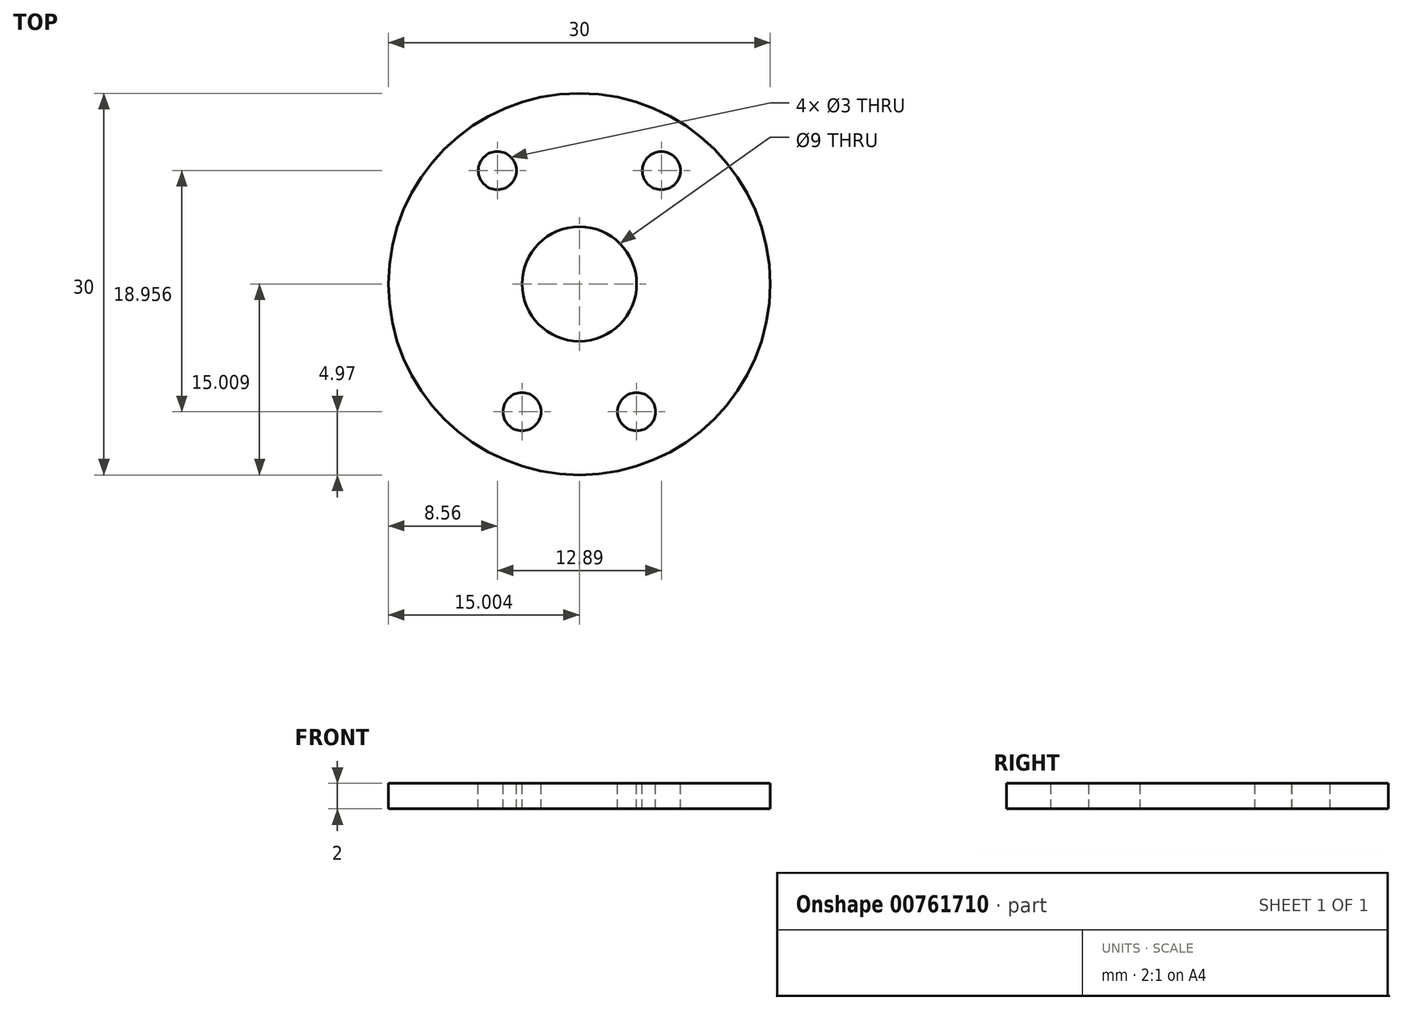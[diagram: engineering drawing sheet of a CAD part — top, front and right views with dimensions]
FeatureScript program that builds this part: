
annotation { "Feature Type Name" : "Feature", "Feature Type Description" : "" }
export const myFeature = defineFeature(function(context is Context, id is Id, definition is map)
    precondition{}
    {
        {
            var Q0;
            Q0=qCreatedBy(makeId("Top.planeOp"),FACE);
            var sketch = newSketch(context, id + "F0", { "sketchPlane" : qUnion([Q0])});
            skCircle(sketch, "E0", {"center": v(0, 0) * mm, "radius": 15 * mm});
            skCircle(sketch, "E1", {"center": v(4.5, -10.03) * mm, "radius": 1.5 * mm});
            skCircle(sketch, "E2", {"center": v(-4.5, -10.03) * mm, "radius": 1.5 * mm});
            skCircle(sketch, "E3.1.0", {"center": v(6.45, 8.92) * mm, "radius": 1.5 * mm});
            skCircle(sketch, "E3.2.1", {"center": v(-6.44, 8.93) * mm, "radius": 1.5 * mm});
            skCircle(sketch, "E4", {"center": v(0, 0) * mm, "radius": 4.5 * mm});
            skArc(sketch, "E5", {"start": v(0, 5) * mm, "mid": v(0, 5) * mm, "end": v(0, 5) * mm, "construction": true});
            skLineSegment(sketch, "E6", {"start": v(-14.15, -5) * mm, "end": v(14.15, -5) * mm});
            skLineSegment(sketch, "E7", {"start": v(-14.14, 5) * mm, "end": v(14.14, 5) * mm});
            skPoint(sketch, "E3.1.1.center.orphan", {"position": v(10.95, 1.13) * mm});
            skPoint(sketch, "E8.1.0.center.orphan", {"position": v(-10.39, -6) * mm});
            skPoint(sketch, "E9.trimOffspring.end.orphan", {"position": v(10.39, -5.99) * mm});
            skPoint(sketch, "E10.orphan", {"position": v(0, 12) * mm});
            skSolve(sketch);
        }
        {
            var Q0;
            Q0 = qSketchRegion(id + "F0", true);
            extrude(context, id + "F1", {"entities" : qUnion([Q0]), "oppositeDirection" : true, "depth" : 2 * mm, "offsetDistance" : 25 * mm});
        }
    });
